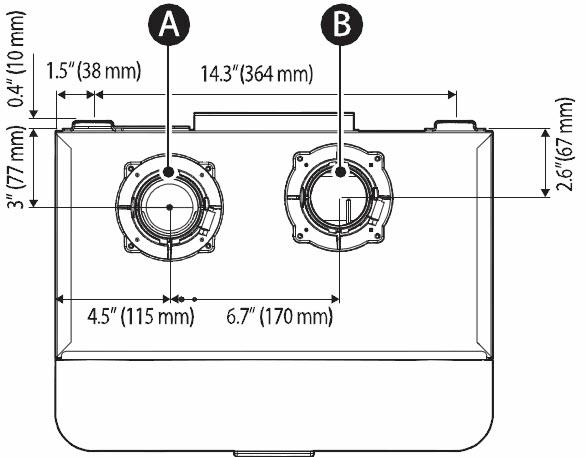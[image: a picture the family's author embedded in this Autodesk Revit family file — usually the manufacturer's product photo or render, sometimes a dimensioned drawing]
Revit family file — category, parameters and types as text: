
# Revit family: Water_Heater-Racks-Navien-NPE-9_Unit_Back_to_Back---
name_source: partatom
category: Mechanical Equipment
revit_build: Autodesk Revit 2016 (Build: 20150220_1215(x64)
units: mm (PartAtom-declared; Revit-internal decimal feet)

## family parameters
Cut with Voids When Loaded = No
Host = Face
OmniClass Number = 23.65.35.11
OmniClass Title = Supply Water Heaters
Part Type = Normal
Room Calculation Point = No
Round Connector Dimension = Use Diameter
Shared = No

## types (4) — shared parameters
2" Exhaust/Intake = Yes
3" Exhaust/Intake = No
Apparent Load = 0 VA
Assembly Code = D3010500
Certifications = Energy Star | AHRI | CSA | CSA | NFS
Cold Water Inlet = 1"
Configuration = NPE_B9_4B2B_3B
Default Elevation = 48 "
Depth = 23.8 "
Description = 9 Unit Back to Back
Exhaust = 2"
Finish = Metal - Navien - White
Flow Rate = 1 GPM
Flow Rate Note = 35°F (19°C) temp rise: 11.2 GPM (42 L/m) | 45°F (25°C) temp rise: 8.7 GPM (33 L/m) | 67°F (36°C) temp rise: NPE-240A: 5.6 GPM(21 L/m), NPE-240S: 5.7 GPM(22 L/m)
Frequency = 60 Hz
Gas Inlet = 1"
Heating Capacity = 120000.0 Btu/h
Heating Capacity Note = 19,900–199,900 (BTU/H)
Height = 65.5 "
Hot Water Outlet = 1"
Ignition = Electronic ignition
Installation Type = Indoor
Intake = 2"
Keynote = 22 33 00.A1
Manifold(s) = (1) 30019039A + (2) 30019042A
Manufacturer = Navien, Inc.
Manufacturer Fax Number = (949) 420-0430
Natural Gas Manifold Pressure = -0.05" WC to -0.58" WC
Natural Gas Supply Pressure = 3.5"–10.5" WC
Number of Poles = 1
Phase = 1
Power Factor = 1
Product Documentation Link = https://www.navieninc.com
Product Name = NPE Series Tankless Water Heaters w/ Racks
Product Page URL = https://www.navieninc.com
Propane Gas Manifold Pressure = -0.10" WC to -0.78" WC
Propane Gas Supply Pressure = 8"–13" WC
Rack(s) = (2) GFFM-KDIZUS-003 + (3) GFFM-KDIZUS-004
Required Cascade Operation Accessory = (9) 30014367A (Common Vent Damper & Cascade Communication Cable) or (8) GXXX000546 (Individual Vent Cascade Communication Cable)
URL = https://www.navieninc.com
Venting = Exhaust: 2" PVC, CPVC, PP, SS / 2" special gas vent type BH (Class II, A/B/C) | Intake: 2" PVC, CPVC, PP, SS / 2" special gas vent type BH (Class II, A/B/C) | Vent clearances: 0" to combustibles
Venting Type = Forced draft direct vent
Version = 2016 - v1.0.a
Voltage = 120 V
Water Pressure = 15–150 PSI
Wi-Fi Ready = NaviLink Wi-Fi Control: PBCM-AS-001
Width = 122.3 "

## per-type parameters (varying)
| type | Constraints | Model | Natural Gas | Propane Gas | Recirculation Inlet | Recirculation Inlet Visibility | Tankless Water Heaters | Weight |
| Natural Gas - Recirculating System - NPE-240A(Advanced)-NG | 6 | (9) NPE-240A-NG | Yes | No | 0" | Yes | (9) NPE-240A-NG | 82.00 lbf |
| Natural Gas - NPE-240S(Standard)-NG | 7 | (9) NPE-240S-NG | Yes | No | 1" | No | (9) NPE-240S-NG | 75.00 lbf |
| Propane Gas - Recirculating System - NPE-240A(Advanced)-LPG | 6 | (9) NPE-240A-LPG | No | Yes | 0" | Yes | (9) NPE-240A-LPG | 82.00 lbf |
| Propane Gas - NPE-240S(Standard)-LPG | 7 | (9) NPE-240S-LPG | No | Yes | 1" | No | (9) NPE-240S-LPG | 75.00 lbf |

## geometry (parser evidence)
native form markers: Sweep x22
no freeform markers — native parametric forms only
